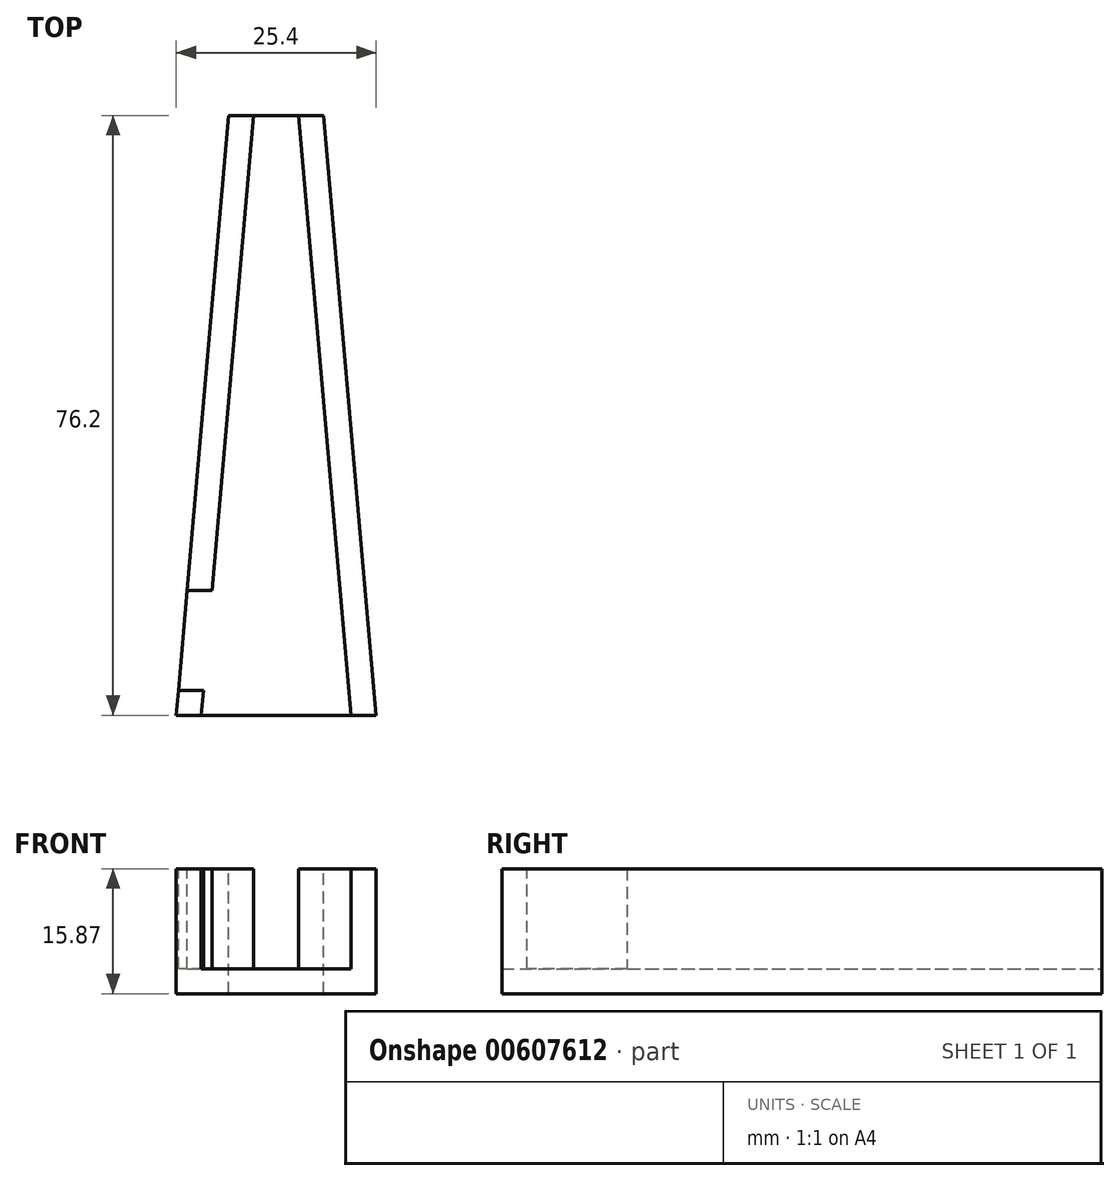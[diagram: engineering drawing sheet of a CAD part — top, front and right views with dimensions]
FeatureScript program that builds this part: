
annotation { "Feature Type Name" : "Feature", "Feature Type Description" : "" }
export const myFeature = defineFeature(function(context is Context, id is Id, definition is map)
    precondition{}
    {
        {
            var Q0;
            Q0=qCreatedBy(makeId("Top.planeOp"),FACE);
            var sketch = newSketch(context, id + "F0", { "sketchPlane" : qUnion([Q0])});
            skLineSegment(sketch, "E0", {"start": v(-12.7, 0) * mm, "end": v(12.7, 0) * mm});
            skLineSegment(sketch, "E1", {"start": v(12.7, 0) * mm, "end": v(6.03, 76.2) * mm});
            skLineSegment(sketch, "E2", {"start": v(6.03, 76.2) * mm, "end": v(-6.03, 76.2) * mm});
            skLineSegment(sketch, "E3", {"start": v(-12.7, 0) * mm, "end": v(-6.03, 76.2) * mm});
            skPoint(sketch, "E4", {"position": v(0, 0) * mm});
            skPoint(sketch, "E5", {"position": v(0, 76.2) * mm});
            skSolve(sketch);
        }
        {
            var Q0;
            Q0 = qSketchRegion(id + "F0", true);
            extrude(context, id + "F1", {"entities" : qUnion([Q0]), "oppositeDirection" : true, "depth" : 3.17 * mm, "offsetDistance" : 25.4 * mm});
        }
        {
            var Q0;
            Q0=makeQuery(id+"F1.opExtrude","CAP_FACE",FACE,{"disambiguationData":[OSD([sQuery(id+"F0.wireOp",EDGE,"E0"),sQuery(id+"F0.wireOp",EDGE,"E1"),sQuery(id+"F0.wireOp",EDGE,"E2"),sQuery(id+"F0.wireOp",EDGE,"E3")])],"isStart":true});
            var sketch = newSketch(context, id + "F2", { "sketchPlane" : qUnion([Q0])});
            skLineSegment(sketch, "E6", {"start": v(-6.03, 76.2) * mm, "end": v(-12.7, 0) * mm});
            skLineSegment(sketch, "E7", {"start": v(-12.7, 0) * mm, "end": v(-9.53, 0) * mm});
            skLineSegment(sketch, "E8", {"start": v(-9.53, 0) * mm, "end": v(-2.86, 76.2) * mm});
            skLineSegment(sketch, "E9", {"start": v(-2.86, 76.2) * mm, "end": v(-6.03, 76.2) * mm});
            skLineSegment(sketch, "E10", {"start": v(6.03, 76.2) * mm, "end": v(12.7, 0) * mm});
            skLineSegment(sketch, "E11", {"start": v(12.7, 0) * mm, "end": v(9.53, 0) * mm});
            skLineSegment(sketch, "E12", {"start": v(9.53, 0) * mm, "end": v(2.86, 76.2) * mm});
            skLineSegment(sketch, "E13", {"start": v(2.86, 76.2) * mm, "end": v(6.03, 76.2) * mm});
            skSolve(sketch);
        }
        {
            var Q0;
            Q0 = qSketchRegion(id + "F2", true);
            extrude(context, id + "F3", {"entities" : qUnion([Q0]), "operationType" : NewBodyOperationType.ADD, "depth" : 12.7 * mm, "offsetDistance" : 25.4 * mm});
        }
        {
            var Q0;
            Q0=makeQuery(id+"F3.opExtrude","CAP_FACE",FACE,{"disambiguationData":[OSD([sQuery(id+"F2.wireOp",EDGE,"E6"),sQuery(id+"F2.wireOp",EDGE,"E7"),sQuery(id+"F2.wireOp",EDGE,"E8"),sQuery(id+"F2.wireOp",EDGE,"E9")])],"isStart":false});
            var sketch = newSketch(context, id + "F4", { "sketchPlane" : qUnion([Q0])});
            skLineSegment(sketch, "E14", {"start": v(-12.7, 0) * mm, "end": v(-6.03, 76.2) * mm, "construction": true});
            skLineSegment(sketch, "E15", {"start": v(12.7, 0) * mm, "end": v(6.03, 76.2) * mm, "construction": true});
            skLineSegment(sketch, "E16", {"start": v(-12.42, 3.18) * mm, "end": v(12.42, 3.18) * mm, "construction": true});
            skLineSegment(sketch, "E17", {"start": v(-11.31, 15.88) * mm, "end": v(11.31, 15.88) * mm, "construction": true});
            skLineSegment(sketch, "E18", {"start": v(-11.31, 15.88) * mm, "end": v(-12.42, 3.18) * mm});
            skLineSegment(sketch, "E19", {"start": v(-12.42, 3.18) * mm, "end": v(0, 3.18) * mm});
            skLineSegment(sketch, "E20", {"start": v(0, 3.18) * mm, "end": v(0, 15.88) * mm});
            skLineSegment(sketch, "E21", {"start": v(0, 15.88) * mm, "end": v(-11.31, 15.88) * mm});
            skSolve(sketch);
        }
        {
            var Q0;
            Q0 = qSketchRegion(id + "F4", true);
            var Q1;
            Q1=makeQuery(id+"F1.opExtrude","CAP_FACE",FACE,{"disambiguationData":[OSD([sQuery(id+"F0.wireOp",EDGE,"E0"),sQuery(id+"F0.wireOp",EDGE,"E1"),sQuery(id+"F0.wireOp",EDGE,"E2"),sQuery(id+"F0.wireOp",EDGE,"E3")])],"isStart":true});
            extrude(context, id + "F5", {"entities" : qUnion([Q0]), "operationType" : NewBodyOperationType.REMOVE, "endBound" : BoundingType.UP_TO_SURFACE, "oppositeDirection" : true, "depth" : 25.4 * mm, "endBoundEntityFace" : qUnion([Q1]), "offsetDistance" : 25.4 * mm});
        }
    });
